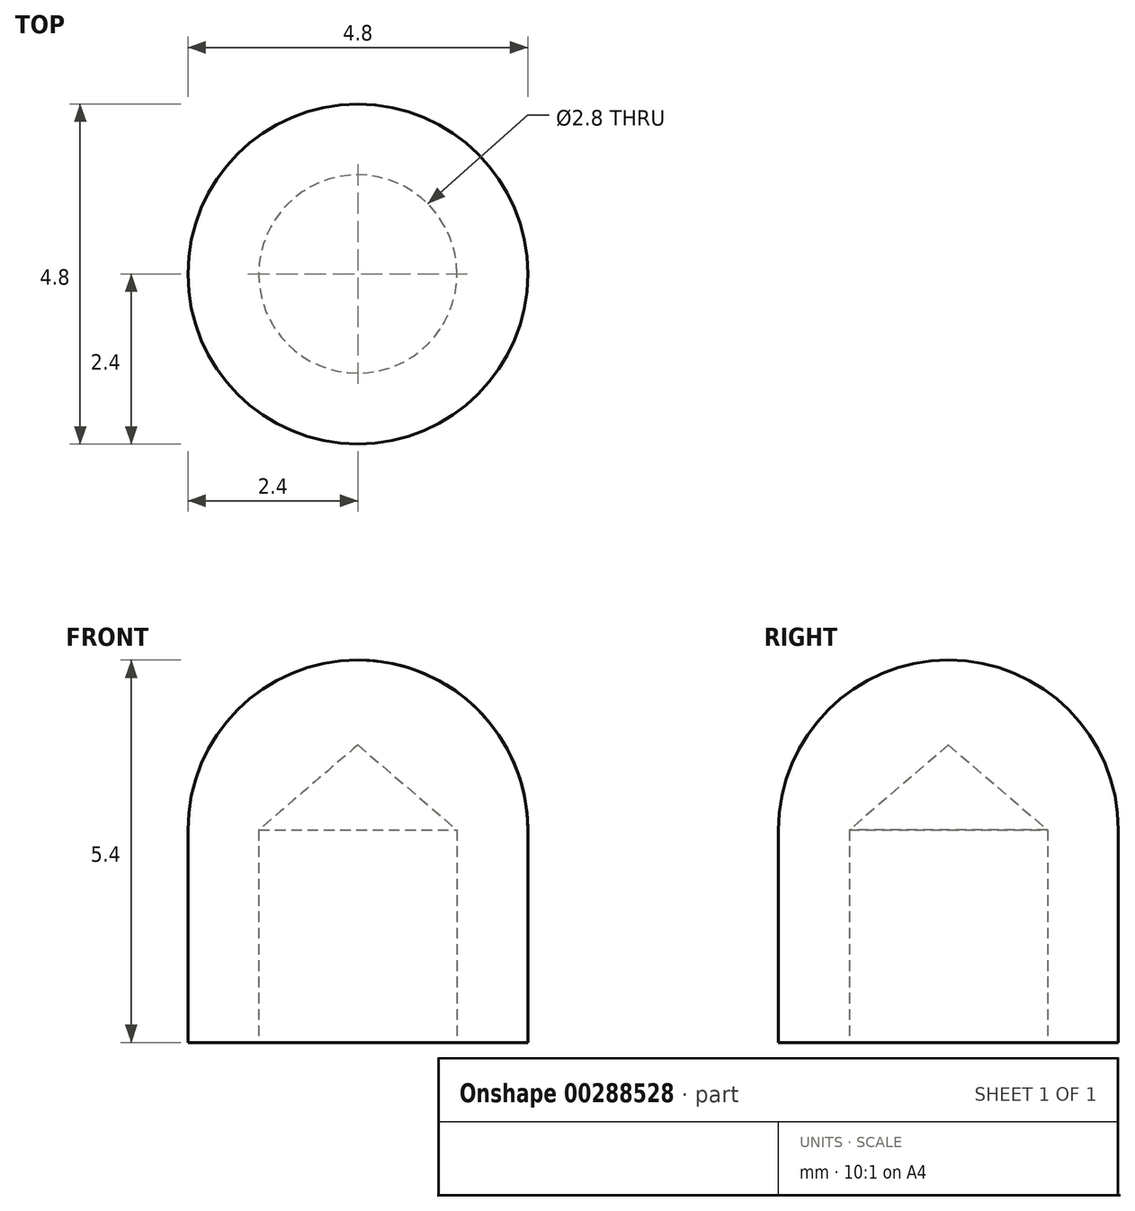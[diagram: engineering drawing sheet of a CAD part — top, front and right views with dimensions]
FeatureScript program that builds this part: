
annotation { "Feature Type Name" : "Feature", "Feature Type Description" : "" }
export const myFeature = defineFeature(function(context is Context, id is Id, definition is map)
    precondition{}
    {
        {
            var Q0;
            Q0=qCreatedBy(makeId("Front.planeOp"),FACE);
            var sketch = newSketch(context, id + "F0", { "sketchPlane" : qUnion([Q0])});
            skLineSegment(sketch, "E0.bottom", {"start": v(0, 0) * mm, "end": v(1.4, 0) * mm, "construction": true});
            skLineSegment(sketch, "E0.top", {"start": v(0, 3) * mm, "end": v(1.4, 3) * mm, "construction": true});
            skLineSegment(sketch, "E0.left", {"start": v(0, 0) * mm, "end": v(0, 3) * mm, "construction": true});
            skLineSegment(sketch, "E0.right", {"start": v(1.4, 0) * mm, "end": v(1.4, 3) * mm});
            skLineSegment(sketch, "E1.0", {"start": v(2.4, 0) * mm, "end": v(2.4, 3) * mm});
            skArc(sketch, "E2", {"start": v(2.4, 3) * mm, "mid": v(1.7, 4.7) * mm, "end": v(0, 5.4) * mm});
            skLineSegment(sketch, "E3", {"start": v(1.4, 0) * mm, "end": v(2.4, 0) * mm});
            skPoint(sketch, "E4", {"position": v(0, 4.2) * mm});
            skLineSegment(sketch, "E5", {"start": v(0, 5.4) * mm, "end": v(0, 4.2) * mm});
            skLineSegment(sketch, "E6", {"start": v(0, 4.2) * mm, "end": v(1.4, 3) * mm});
            skSolve(sketch);
        }
        {
            var Q0;
            Q0=makeQuery(id+"F0.imprint","IMPRINT",FACE,{"disambiguationData":[TD([[makeQuery(id+"F0.imprint","IMPRINT",EDGE,{"derivedFrom":sQuery(id+"F0.wireOp",EDGE,"E0.right")}),-1.0]])]});
            var Q1;
            Q1=sQuery(id+"F0.wireOp",EDGE,"E0.left");
            revolve(context, id + "F1", {"entities" : qUnion([Q0]), "axis" : qUnion([Q1]), "revolveType" : RevolveType.FULL});
        }
    });
